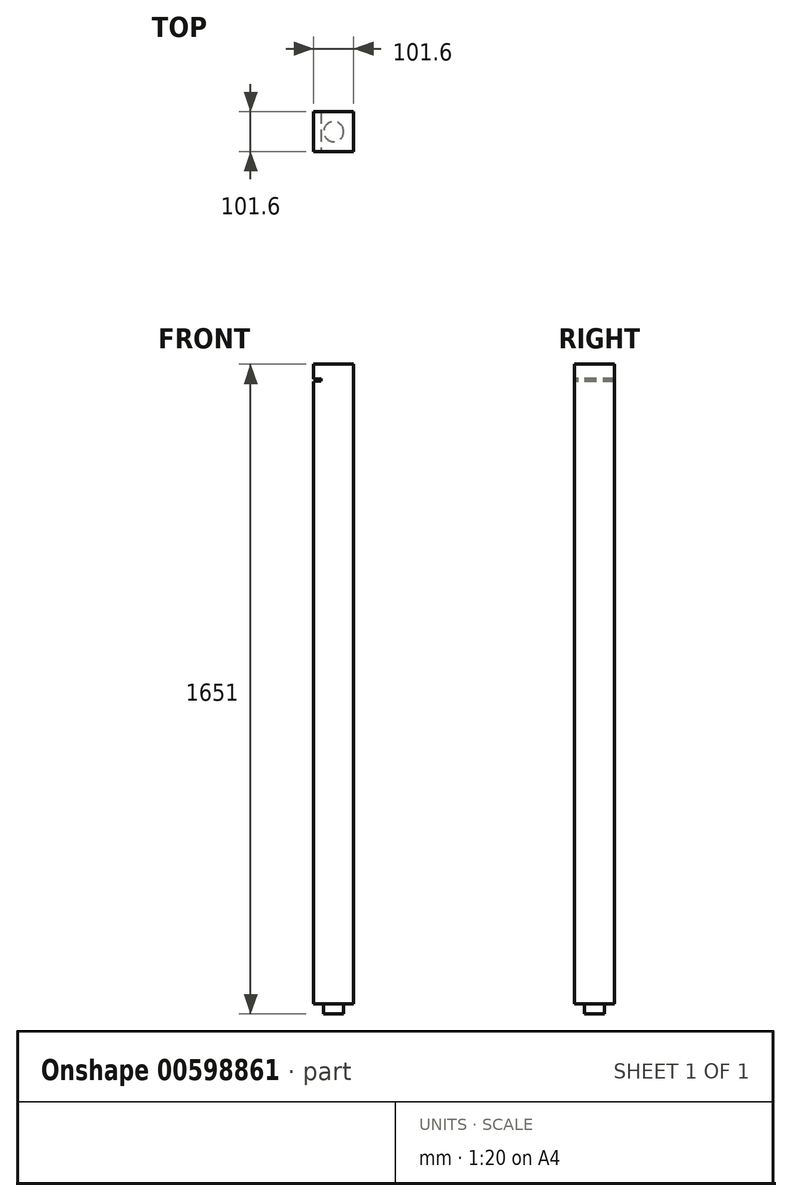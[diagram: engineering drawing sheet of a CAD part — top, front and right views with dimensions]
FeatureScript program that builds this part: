
annotation { "Feature Type Name" : "Feature", "Feature Type Description" : "" }
export const myFeature = defineFeature(function(context is Context, id is Id, definition is map)
    precondition{}
    {
        {
            var Q0;
            Q0=qCreatedBy(makeId("Top.planeOp"),FACE);
            var sketch = newSketch(context, id + "F0", { "sketchPlane" : qUnion([Q0])});
            skCircle(sketch, "E0", {"center": v(0, 0) * mm, "radius": 25.4 * mm});
            skSolve(sketch);
        }
        {
            var Q0;
            Q0 = qSketchRegion(id + "F0", true);
            extrude(context, id + "F1", {"entities" : qUnion([Q0]), "depth" : 25.4 * mm, "offsetDistance" : 25.4 * mm});
        }
        {
            var Q0;
            Q0=makeQuery(id+"F1.opExtrude","CAP_FACE",FACE,{"disambiguationData":[OSD([sQuery(id+"F0.wireOp",EDGE,"E0")])],"isStart":false});
            var sketch = newSketch(context, id + "F2", { "sketchPlane" : qUnion([Q0])});
            skLineSegment(sketch, "E1", {"start": v(0, 0) * mm, "end": v(-50.8, 0) * mm});
            skLineSegment(sketch, "E2", {"start": v(-50.8, 0) * mm, "end": v(-50.8, 50.8) * mm});
            skLineSegment(sketch, "E3.bottom", {"start": v(-50.8, 50.8) * mm, "end": v(50.8, 50.8) * mm});
            skLineSegment(sketch, "E3.top", {"start": v(-50.8, -50.8) * mm, "end": v(50.8, -50.8) * mm});
            skLineSegment(sketch, "E3.left", {"start": v(-50.8, 50.8) * mm, "end": v(-50.8, -50.8) * mm});
            skLineSegment(sketch, "E3.right", {"start": v(50.8, 50.8) * mm, "end": v(50.8, -50.8) * mm});
            skSolve(sketch);
        }
        {
            var Q0;
            Q0 = qSketchRegion(id + "F2", true);
            extrude(context, id + "F3", {"entities" : qUnion([Q0]), "operationType" : NewBodyOperationType.ADD, "depth" : 1625.6 * mm, "offsetDistance" : 25.4 * mm});
        }
        {
            var Q0;
            Q0=makeQuery(id+"F3.opExtrude","SWEPT_FACE",FACE,{"disambiguationData":[OSD([sQuery(id+"F2.wireOp",EDGE,"E3.top")])]});
            var sketch = newSketch(context, id + "F4", { "sketchPlane" : qUnion([Q0])});
            skLineSegment(sketch, "E4", {"start": v(-50.8, 1651) * mm, "end": v(-50.8, 1612.9) * mm});
            skLineSegment(sketch, "E5", {"start": v(-23.35, 1651) * mm, "end": v(-23.35, 1614.17) * mm});
            skLineSegment(sketch, "E6", {"start": v(-23.35, 1614.17) * mm, "end": v(-50.8, 1614.17) * mm});
            skLineSegment(sketch, "E7", {"start": v(-50.8, 1612.9) * mm, "end": v(-32.12, 1614.17) * mm});
            skLineSegment(sketch, "E8", {"start": v(-32.12, 1614.17) * mm, "end": v(-31.7, 1607.83) * mm});
            skLineSegment(sketch, "E9", {"start": v(-31.7, 1607.83) * mm, "end": v(-50.8, 1606.54) * mm});
            skSolve(sketch);
        }
        {
            var Q0;
            {var subQ0=sQuery(id+"F4.wireOp",EDGE,"E7");Q0=makeQuery(id+"F4.imprint","IMPRINT",FACE,{"disambiguationData":[TD([[makeQuery(id+"F4.imprint","IMPRINT",EDGE,{"derivedFrom":subQ0}),-1.0]])]});}
            extrude(context, id + "F5", {"entities" : qUnion([Q0]), "operationType" : NewBodyOperationType.REMOVE, "oppositeDirection" : true, "depth" : 101.6 * mm, "offsetDistance" : 25.4 * mm});
        }
    });
